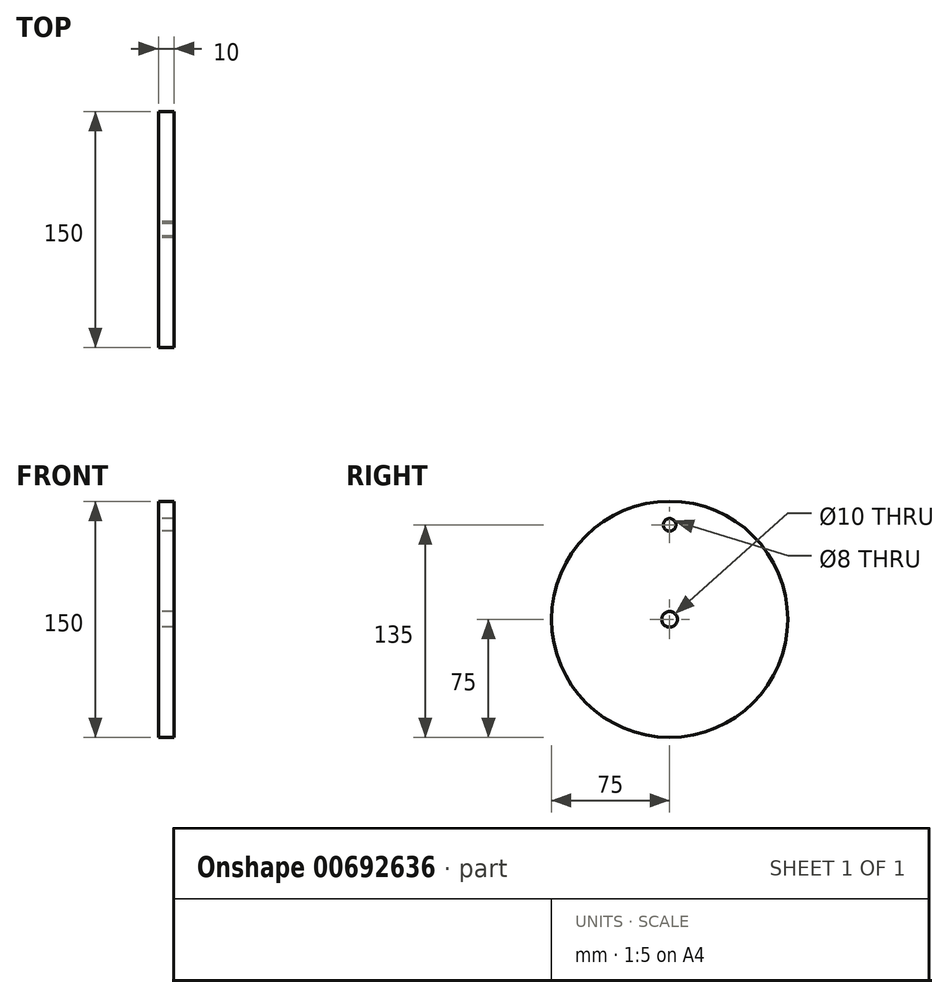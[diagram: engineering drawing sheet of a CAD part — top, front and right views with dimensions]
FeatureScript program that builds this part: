
annotation { "Feature Type Name" : "Feature", "Feature Type Description" : "" }
export const myFeature = defineFeature(function(context is Context, id is Id, definition is map)
    precondition{}
    {
        {
            var Q0;
            Q0=qCreatedBy(makeId("Right.planeOp"),FACE);
            var sketch = newSketch(context, id + "F0", { "sketchPlane" : qUnion([Q0])});
            skCircle(sketch, "E0", {"center": v(0, 0) * mm, "radius": 75 * mm});
            skCircle(sketch, "E1", {"center": v(0, 0) * mm, "radius": 5 * mm});
            skCircle(sketch, "E2", {"center": v(0, 60) * mm, "radius": 4 * mm});
            skSolve(sketch);
        }
        {
            var Q0;
            Q0=makeQuery(id+"F0.imprint","IMPRINT",FACE,{"disambiguationData":[TD([[makeQuery(id+"F0.imprint","IMPRINT",EDGE,{"derivedFrom":sQuery(id+"F0.wireOp",EDGE,"E0")}),1.0]])]});
            extrude(context, id + "F1", {"entities" : qUnion([Q0]), "depth" : 10 * mm, "offsetDistance" : 25 * mm});
        }
    });
